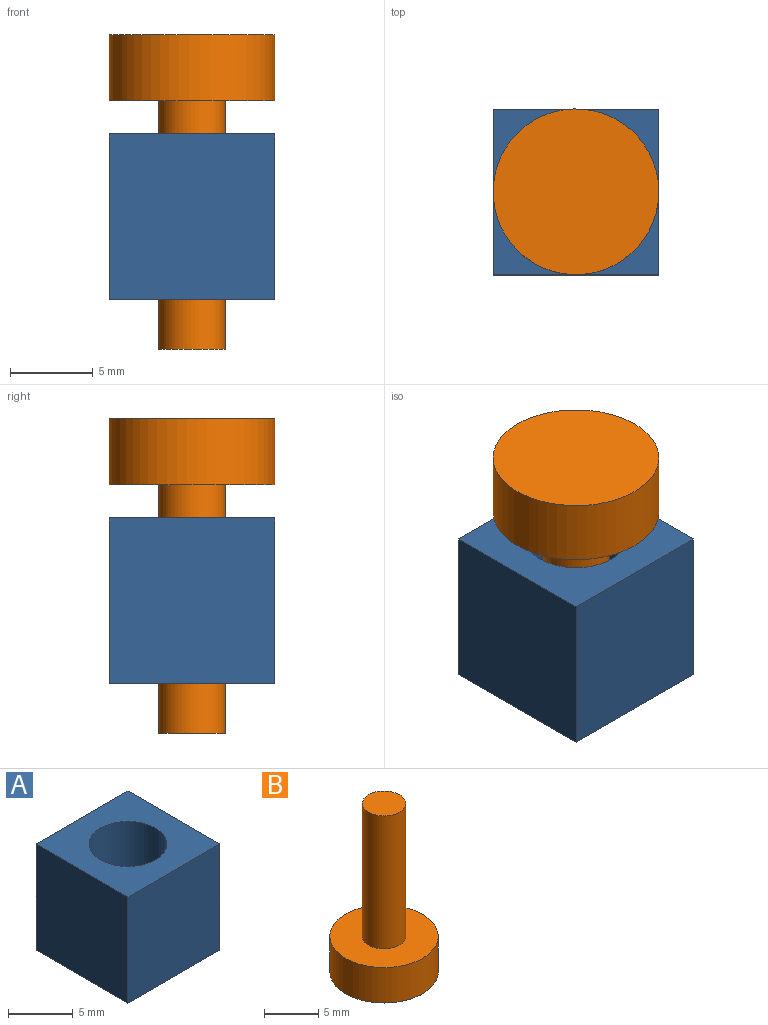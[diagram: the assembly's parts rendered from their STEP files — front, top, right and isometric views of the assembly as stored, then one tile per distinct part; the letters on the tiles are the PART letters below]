
ASSEMBLY  parts=2 mates=1
PART A: 7 faces, bbox 10x10x10 mm
  f0: plane 10x10mm, normal (0,1,0), area 100mm2, adj f1,f3,f4,f5
  f1: plane 10x10mm, normal (-1,0,0), area 100mm2, adj f0,f2,f4,f5
  f2: plane 10x10mm, normal (0,-1,0), area 100mm2, adj f1,f3,f4,f5
  f3: plane 10x10mm, normal (1,0,0), area 100mm2, adj f0,f2,f4,f5
  f4: plane 10x10mm, normal (0,0,1), area 71.7mm2, adj f0,f1,f2,f3,f6
  f5: plane 10x10mm, normal (0,0,-1), area 71.7mm2, adj f0,f1,f2,f3,f6
  f6: cylinder r=3mm len=10mm, axis (0,0,1), area 188.5mm2, adj f4,f5
PART B: 5 faces, bbox 10x10x19 mm
  f0: cylinder r=5mm len=10mm, axis (0,0,-1), area 125.7mm2, adj f1,f2
  f1: plane 10x10mm, normal (0,0,1), area 66mm2, adj f0,f3
  f2: plane 10x10mm, normal (0,0,-1), area 78.5mm2, adj f0
  f3: cylinder r=2mm len=15mm, axis (0,0,-1), area 188.5mm2, adj f1,f4
  f4: plane 4x4mm, normal (0,0,1), area 12.6mm2, adj f3
PLACE A at identity
PLACE B rot(axis=(1,0,0),180deg) t=(0,0,16)mm
MATE slider B.f3 <-> A.f6  axis (0,0,-1) through (0,0,12)mm
